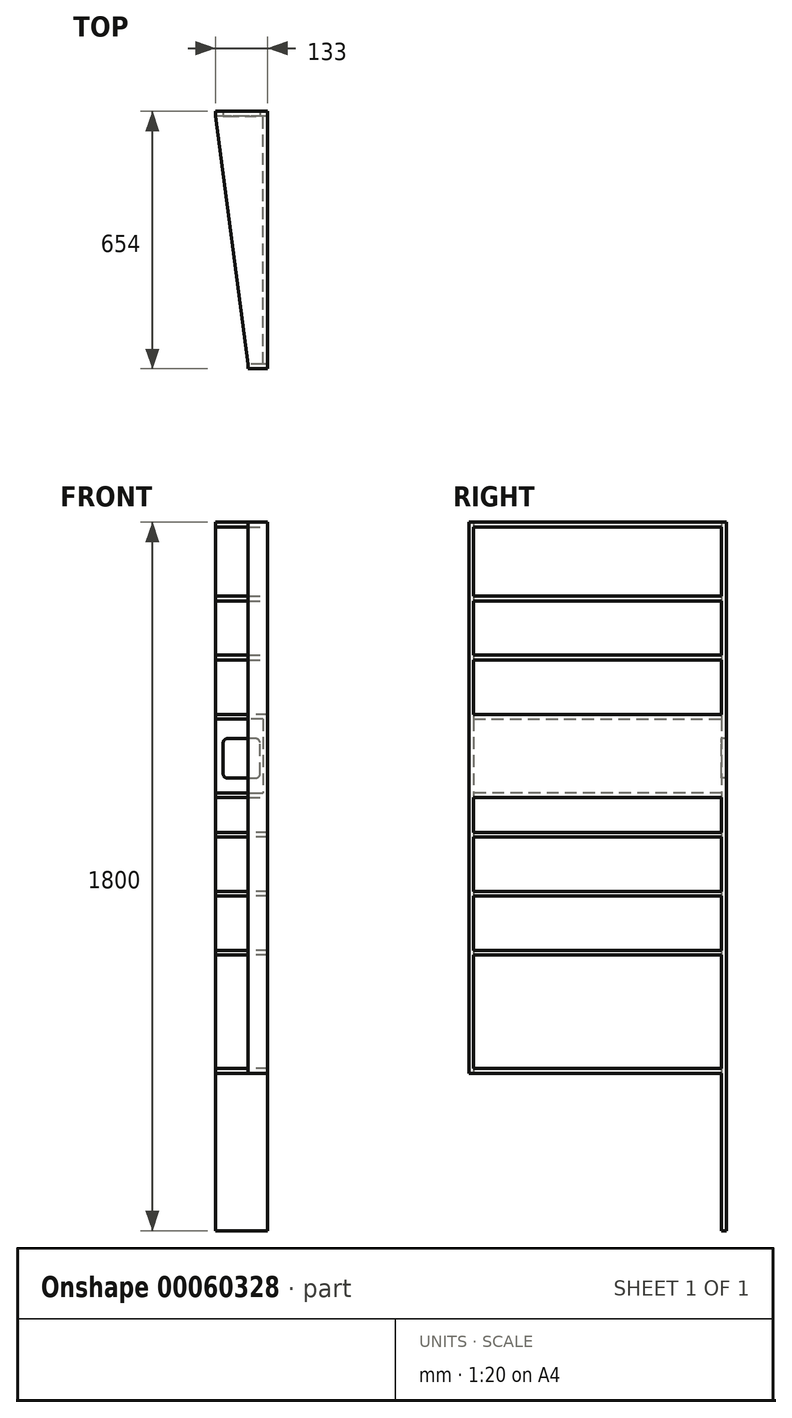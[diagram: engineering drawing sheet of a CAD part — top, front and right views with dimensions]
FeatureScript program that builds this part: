
annotation { "Feature Type Name" : "Feature", "Feature Type Description" : "" }
export const myFeature = defineFeature(function(context is Context, id is Id, definition is map)
    precondition{}
    {
        {
            var Q0;
            Q0=qCreatedBy(makeId("Front.planeOp"),FACE);
            var sketch = newSketch(context, id + "F0", { "sketchPlane" : qUnion([Q0])});
            skLineSegment(sketch, "E0", {"start": v(0, 0) * mm, "end": v(-133, 0) * mm});
            skLineSegment(sketch, "E1", {"start": v(-103, 1150) * mm, "end": v(-30, 1150) * mm});
            skLineSegment(sketch, "E2", {"start": v(-20, 1160) * mm, "end": v(-20, 1240) * mm});
            skLineSegment(sketch, "E3", {"start": v(-30, 1250) * mm, "end": v(-103, 1250) * mm});
            skLineSegment(sketch, "E4", {"start": v(-133, 1800) * mm, "end": v(0, 1800) * mm});
            skLineSegment(sketch, "E5", {"start": v(0, 0) * mm, "end": v(0, 1800) * mm});
            skPoint(sketch, "E6.visualSharp", {"position": v(-20, 1150) * mm});
            skArc(sketch, "E6.filletArc", {"start": v(-30, 1150) * mm, "mid": v(-22.93, 1152.93) * mm, "end": v(-20, 1160) * mm});
            skPoint(sketch, "E7.visualSharp", {"position": v(-20, 1250) * mm});
            skArc(sketch, "E7.filletArc", {"start": v(-20, 1240) * mm, "mid": v(-22.93, 1247.07) * mm, "end": v(-30, 1250) * mm});
            skLineSegment(sketch, "E8", {"start": v(-113, 1240) * mm, "end": v(-113, 1160) * mm});
            skLineSegment(sketch, "E9", {"start": v(-133, 1800) * mm, "end": v(-133, 0) * mm});
            skPoint(sketch, "E10.visualSharp", {"position": v(-113, 1250) * mm});
            skArc(sketch, "E10.filletArc", {"start": v(-103, 1250) * mm, "mid": v(-110.07, 1247.07) * mm, "end": v(-113, 1240) * mm});
            skPoint(sketch, "E11.visualSharp", {"position": v(-113, 1150) * mm});
            skArc(sketch, "E11.filletArc", {"start": v(-113, 1160) * mm, "mid": v(-110.07, 1152.93) * mm, "end": v(-103, 1150) * mm});
            skSolve(sketch);
        }
        {
            var Q0;
            Q0=qCreatedBy(makeId("Top.planeOp"),FACE);
            var sketch = newSketch(context, id + "F1", { "sketchPlane" : qUnion([Q0])});
            skLineSegment(sketch, "E12", {"start": v(0, 0) * mm, "end": v(0, -630) * mm});
            skLineSegment(sketch, "E13", {"start": v(0, -630) * mm, "end": v(-50, -630) * mm});
            skLineSegment(sketch, "E14", {"start": v(-50, -630) * mm, "end": v(-133, 0) * mm});
            skLineSegment(sketch, "E15", {"start": v(-133, 0) * mm, "end": v(-133, -630) * mm});
            skLineSegment(sketch, "E16", {"start": v(-133, -630) * mm, "end": v(-50, -630) * mm});
            skLineSegment(sketch, "E17", {"start": v(-133, 0) * mm, "end": v(0, 0) * mm});
            skLineSegment(sketch, "E18.top", {"start": v(0, -642) * mm, "end": v(-50, -642) * mm});
            skLineSegment(sketch, "E18.left", {"start": v(0, -630) * mm, "end": v(0, -642) * mm});
            skLineSegment(sketch, "E18.right", {"start": v(-50, -630) * mm, "end": v(-50, -642) * mm});
            skSolve(sketch);
        }
        {
            var Q0;
            Q0=makeQuery(id+"F0.imprint","IMPRINT",FACE,{"disambiguationData":[TD([[makeQuery(id+"F0.imprint","IMPRINT",EDGE,{"derivedFrom":sQuery(id+"F0.wireOp",EDGE,"E0")}),-1.0]])]});
            extrude(context, id + "F2", {"entities" : qUnion([Q0]), "oppositeDirection" : true, "depth" : 12 * mm});
        }
        {
            var Q0;
            Q0=makeQuery(id+"F2.opExtrude","CAP_FACE",FACE,{"disambiguationData":[OSD([sQuery(id+"F0.wireOp",EDGE,"E0"),sQuery(id+"F0.wireOp",EDGE,"t0fPLE5H-aFwR-Tiys-TCuq-BQvsl80l82CM"),sQuery(id+"F0.wireOp",EDGE,"E1"),sQuery(id+"F0.wireOp",EDGE,"E2"),sQuery(id+"F0.wireOp",EDGE,"E3"),sQuery(id+"F0.wireOp",EDGE,"eRWxVB1K-2oxu-OcZY-zab4-DF47jyrMNdGK"),sQuery(id+"F0.wireOp",EDGE,"E4"),sQuery(id+"F0.wireOp",EDGE,"E5"),sQuery(id+"F0.wireOp",EDGE,"E6.filletArc"),sQuery(id+"F0.wireOp",EDGE,"E7.filletArc")])],"isStart":true});
            var sketch = newSketch(context, id + "F3", { "sketchPlane" : qUnion([Q0])});
            skLineSegment(sketch, "E19.bottom", {"start": v(0, 412) * mm, "end": v(-133, 412) * mm});
            skLineSegment(sketch, "E19.top", {"start": v(0, 400) * mm, "end": v(-133, 400) * mm});
            skLineSegment(sketch, "E19.left", {"start": v(0, 412) * mm, "end": v(0, 400) * mm});
            skLineSegment(sketch, "E19.right", {"start": v(-133, 412) * mm, "end": v(-133, 400) * mm});
            skLineSegment(sketch, "E20.bottom", {"start": v(0, 850) * mm, "end": v(-133, 850) * mm});
            skLineSegment(sketch, "E20.top", {"start": v(0, 862) * mm, "end": v(-133, 862) * mm});
            skLineSegment(sketch, "E20.left", {"start": v(0, 850) * mm, "end": v(0, 862) * mm});
            skLineSegment(sketch, "E20.right", {"start": v(-133, 850) * mm, "end": v(-133, 862) * mm});
            skLineSegment(sketch, "E21.bottom", {"start": v(0, 700) * mm, "end": v(-133, 700) * mm});
            skLineSegment(sketch, "E21.top", {"start": v(0, 712) * mm, "end": v(-133, 712) * mm});
            skLineSegment(sketch, "E21.left", {"start": v(0, 700) * mm, "end": v(0, 712) * mm});
            skLineSegment(sketch, "E21.right", {"start": v(-133, 700) * mm, "end": v(-133, 712) * mm});
            skLineSegment(sketch, "E22.bottom", {"start": v(0, 1000) * mm, "end": v(-133, 1000) * mm});
            skLineSegment(sketch, "E22.top", {"start": v(0, 1012) * mm, "end": v(-133, 1012) * mm});
            skLineSegment(sketch, "E22.left", {"start": v(0, 1000) * mm, "end": v(0, 1012) * mm});
            skLineSegment(sketch, "E22.right", {"start": v(-133, 1000) * mm, "end": v(-133, 1012) * mm});
            skLineSegment(sketch, "E23.bottom", {"start": v(0, 1300) * mm, "end": v(-133, 1300) * mm});
            skLineSegment(sketch, "E23.top", {"start": v(0, 1312) * mm, "end": v(-133, 1312) * mm});
            skLineSegment(sketch, "E23.left", {"start": v(0, 1300) * mm, "end": v(0, 1312) * mm});
            skLineSegment(sketch, "E23.right", {"start": v(-133, 1300) * mm, "end": v(-133, 1312) * mm});
            skLineSegment(sketch, "E24.bottom", {"start": v(-133, 1462) * mm, "end": v(0, 1462) * mm});
            skLineSegment(sketch, "E24.top", {"start": v(-133, 1450) * mm, "end": v(0, 1450) * mm});
            skLineSegment(sketch, "E24.left", {"start": v(-133, 1462) * mm, "end": v(-133, 1450) * mm});
            skLineSegment(sketch, "E24.right", {"start": v(0, 1462) * mm, "end": v(0, 1450) * mm});
            skLineSegment(sketch, "E25.bottom", {"start": v(-133, 1612) * mm, "end": v(0, 1612) * mm});
            skLineSegment(sketch, "E25.top", {"start": v(-133, 1600) * mm, "end": v(0, 1600) * mm});
            skLineSegment(sketch, "E25.left", {"start": v(-133, 1612) * mm, "end": v(-133, 1600) * mm});
            skLineSegment(sketch, "E25.right", {"start": v(0, 1612) * mm, "end": v(0, 1600) * mm});
            skLineSegment(sketch, "E26.bottom", {"start": v(-133, 1788) * mm, "end": v(0, 1788) * mm});
            skLineSegment(sketch, "E26.top", {"start": v(-133, 1800) * mm, "end": v(0, 1800) * mm});
            skLineSegment(sketch, "E26.left", {"start": v(-133, 1788) * mm, "end": v(-133, 1800) * mm});
            skLineSegment(sketch, "E26.right", {"start": v(0, 1788) * mm, "end": v(0, 1800) * mm});
            skLineSegment(sketch, "E27.bottom", {"start": v(-133, 1100) * mm, "end": v(0, 1100) * mm});
            skLineSegment(sketch, "E27.top", {"start": v(-133, 1112) * mm, "end": v(0, 1112) * mm});
            skLineSegment(sketch, "E27.left", {"start": v(-133, 1100) * mm, "end": v(-133, 1112) * mm});
            skLineSegment(sketch, "E27.right", {"start": v(0, 1100) * mm, "end": v(0, 1112) * mm});
            skLineSegment(sketch, "E28.bottom", {"start": v(-12, 1300) * mm, "end": v(0, 1300) * mm});
            skLineSegment(sketch, "E28.top", {"start": v(-12, 1112) * mm, "end": v(0, 1112) * mm});
            skLineSegment(sketch, "E28.left", {"start": v(-12, 1300) * mm, "end": v(-12, 1112) * mm});
            skLineSegment(sketch, "E28.right", {"start": v(0, 1300) * mm, "end": v(0, 1112) * mm});
            skSolve(sketch);
        }
        {
            var Q0;
            Q0=qSketchRegion(id+"F3",true);
            extrude(context, id + "F4", {"entities" : qUnion([Q0]), "operationType" : NewBodyOperationType.ADD, "depth" : 630 * mm});
        }
        {
            var Q0;
            Q0=makeQuery(id+"F1.imprint","IMPRINT",FACE,{"disambiguationData":[TD([[makeQuery(id+"F1.imprint","IMPRINT",EDGE,{"derivedFrom":sQuery(id+"F1.wireOp",EDGE,"E14")}),1.0]])]});
            extrude(context, id + "F5", {"entities" : qUnion([Q0]), "operationType" : NewBodyOperationType.REMOVE, "endBound" : BoundingType.THROUGH_ALL, "depth" : 25 * mm});
        }
        {
            var Q0;
            Q0=makeQuery(id+"F1.imprint","IMPRINT",FACE,{"disambiguationData":[TD([[makeQuery(id+"F1.imprint","IMPRINT",EDGE,{"derivedFrom":sQuery(id+"F1.wireOp",EDGE,"E13")}),1.0]])]});
            extrude(context, id + "F6", {"entities" : qUnion([Q0]), "operationType" : NewBodyOperationType.ADD, "depth" : 1800 * mm, "hasSecondDirection" : true, "secondDirectionOppositeDirection" : false, "secondDirectionDepth" : 400 * mm});
        }
        {
            var Q0;
            Q0=makeQuery(id+"F2.opExtrude","SWEPT_BODY",BODY,{"disambiguationData":[OSD([sQuery(id+"F0.wireOp",EDGE,"E0"),sQuery(id+"F0.wireOp",EDGE,"E1"),sQuery(id+"F0.wireOp",EDGE,"E2"),sQuery(id+"F0.wireOp",EDGE,"E3"),sQuery(id+"F0.wireOp",EDGE,"E4"),sQuery(id+"F0.wireOp",EDGE,"E5"),sQuery(id+"F0.wireOp",EDGE,"E6.filletArc"),sQuery(id+"F0.wireOp",EDGE,"E7.filletArc"),sQuery(id+"F0.wireOp",EDGE,"E8"),sQuery(id+"F0.wireOp",EDGE,"E9"),sQuery(id+"F0.wireOp",EDGE,"E10.filletArc"),sQuery(id+"F0.wireOp",EDGE,"E11.filletArc")])]});
            transform(context, id + "F7", {"entities" : qUnion([Q0]), "transformType" : TransformType.TRANSLATION_3D, "dx" : 0 * mm, "dy" : 0 * mm, "dz" : 0 * mm, "makeCopy" : true});
        }
        {
            var Q0;
            Q0=makeQuery(id+"F7.opPattern","COPY",BODY,{"derivedFrom":makeQuery(id+"F2.opExtrude","SWEPT_BODY",BODY,{"disambiguationData":[OSD([sQuery(id+"F0.wireOp",EDGE,"E0"),sQuery(id+"F0.wireOp",EDGE,"E1"),sQuery(id+"F0.wireOp",EDGE,"E2"),sQuery(id+"F0.wireOp",EDGE,"E3"),sQuery(id+"F0.wireOp",EDGE,"E4"),sQuery(id+"F0.wireOp",EDGE,"E5"),sQuery(id+"F0.wireOp",EDGE,"E6.filletArc"),sQuery(id+"F0.wireOp",EDGE,"E7.filletArc"),sQuery(id+"F0.wireOp",EDGE,"E8"),sQuery(id+"F0.wireOp",EDGE,"E9"),sQuery(id+"F0.wireOp",EDGE,"E10.filletArc"),sQuery(id+"F0.wireOp",EDGE,"E11.filletArc")])]}),"instanceName":"1"});
            deleteBodies(context, id + "F8", {"entities" : qUnion([Q0])});
        }
    });
